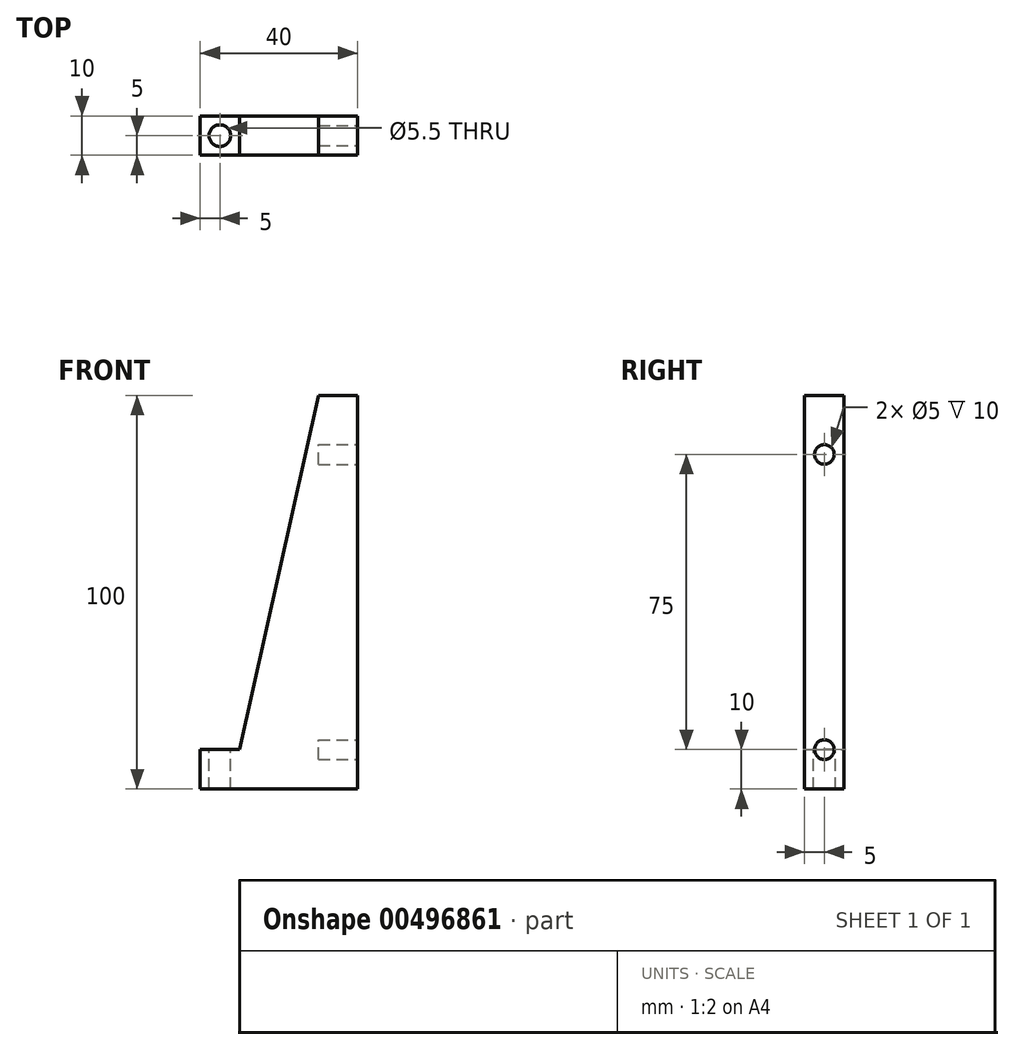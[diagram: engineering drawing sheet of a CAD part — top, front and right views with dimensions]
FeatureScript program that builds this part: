
annotation { "Feature Type Name" : "Feature", "Feature Type Description" : "" }
export const myFeature = defineFeature(function(context is Context, id is Id, definition is map)
    precondition{}
    {
        {
            var Q0;
            Q0=qCreatedBy(makeId("Front.planeOp"),FACE);
            var sketch = newSketch(context, id + "F0", { "sketchPlane" : qUnion([Q0])});
            skLineSegment(sketch, "E0", {"start": v(0, 0) * mm, "end": v(40, 0) * mm});
            skLineSegment(sketch, "E1", {"start": v(40, 0) * mm, "end": v(40, 100) * mm});
            skLineSegment(sketch, "E2", {"start": v(0, 0) * mm, "end": v(0, 10) * mm});
            skLineSegment(sketch, "E3", {"start": v(0, 10) * mm, "end": v(10, 10) * mm});
            skLineSegment(sketch, "E4", {"start": v(10, 10) * mm, "end": v(30, 100) * mm});
            skLineSegment(sketch, "E5", {"start": v(30, 100) * mm, "end": v(40, 100) * mm});
            skSolve(sketch);
        }
        {
            var Q0;
            Q0 = qSketchRegion(id + "F0", true);
            extrude(context, id + "F1", {"entities" : qUnion([Q0]), "depth" : 10 * mm});
        }
        {
            var Q0;
            Q0=makeQuery(id+"F1.opExtrude","SWEPT_FACE",FACE,{"disambiguationData":[OSD([sQuery(id+"F0.wireOp",EDGE,"E3")])]});
            var sketch = newSketch(context, id + "F2", { "sketchPlane" : qUnion([Q0])});
            skCircle(sketch, "E6", {"center": v(5, -5) * mm, "radius": 2.75 * mm});
            skSolve(sketch);
        }
        {
            var Q0;
            Q0 = qSketchRegion(id + "F2", true);
            extrude(context, id + "F3", {"entities" : qUnion([Q0]), "operationType" : NewBodyOperationType.REMOVE, "oppositeDirection" : true, "depth" : 25 * mm});
        }
        {
            var Q0;
            Q0=makeQuery(id+"F1.opExtrude","SWEPT_FACE",FACE,{"disambiguationData":[OSD([sQuery(id+"F0.wireOp",EDGE,"E1")])]});
            var sketch = newSketch(context, id + "F4", { "sketchPlane" : qUnion([Q0])});
            skCircle(sketch, "E7", {"center": v(-5, 85) * mm, "radius": 2.5 * mm});
            skCircle(sketch, "E8", {"center": v(-5, 10) * mm, "radius": 2.5 * mm});
            skSolve(sketch);
        }
        {
            var Q0;
            Q0 = qSketchRegion(id + "F4", true);
            extrude(context, id + "F5", {"entities" : qUnion([Q0]), "operationType" : NewBodyOperationType.REMOVE, "oppositeDirection" : true, "depth" : 10 * mm});
        }
    });
